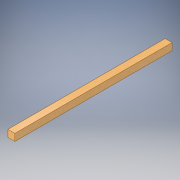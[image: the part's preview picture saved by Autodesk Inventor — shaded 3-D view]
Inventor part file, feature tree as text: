
AUTODESK INVENTOR PART (.ipt)
format: ipt  version: 2019 (Build 230136000, 136)  size: 113,152 bytes
history: native  units: mm
features: other x4, extrude x1, sketch x1
ambient origin geometry x8: Origin, YZ Plane, XZ Plane, XY Plane, X Axis, Y Axis, Z Axis, Center Point
bodies: Body1 (feature_tree)
feature tree (6):
  other  "Таблица"
  other  "Балясина-01"
  other  "Балясина-02"
  other  "Твердое тело1"
  extrude  "Выдавливание1"  TaperAngle=0.0deg  [1 undecoded]
  sketch  "Эскиз1"
note: 1 required parameter value undecoded (feature->parameter linkage not recoverable at this tier; creation-order binding heuristic only, values carry confidence <= 0.55)
